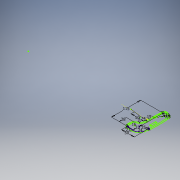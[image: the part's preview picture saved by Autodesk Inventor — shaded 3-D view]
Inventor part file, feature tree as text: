
AUTODESK INVENTOR PART (.ipt)
format: ipt  version: 2019.2 (Build 232265000, 265)  size: 243,712 bytes
history: native  units: mm
features: sketch x1
ambient origin geometry x8: Origin, YZ Plane, XZ Plane, XY Plane, X Axis, Y Axis, Z Axis, Center Point
feature tree (1):
  sketch  "Sketch1"  dims[d0=6.0mm d1=6.0mm d2=33.0mm d3=50.0mm d4=24.0mm d5=21.0mm d6=50.0mm d10=27.0mm d11=6.0mm d12=28.0mm d13=16.0mm d14=74.0mm d15=15.0mm d16=115.0mm d17=25.0mm d18=32.0mm d19=19.0mm d20=7.5mm d22=500.0mm]
